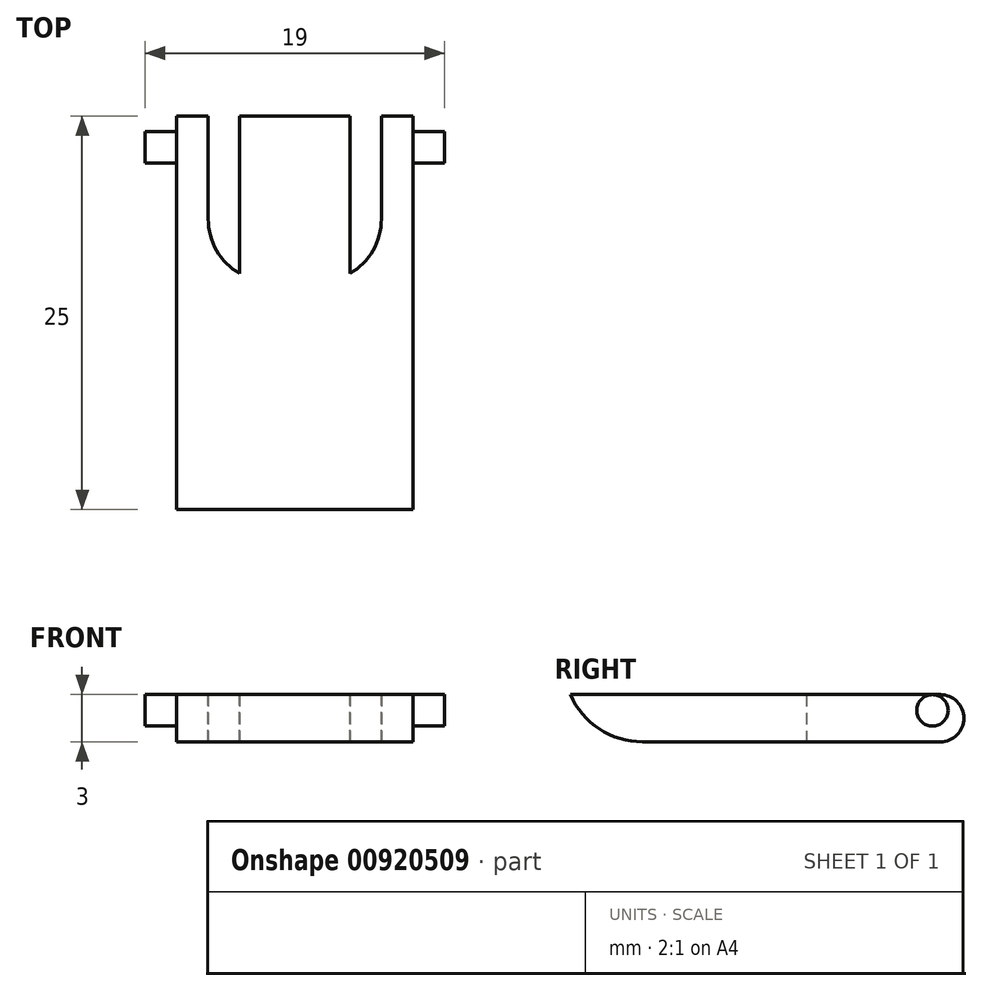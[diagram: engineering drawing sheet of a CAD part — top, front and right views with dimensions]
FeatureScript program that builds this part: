
annotation { "Feature Type Name" : "Feature", "Feature Type Description" : "" }
export const myFeature = defineFeature(function(context is Context, id is Id, definition is map)
    precondition{}
    {
        {
            var Q0;
            Q0=qCreatedBy(makeId("Top.planeOp"),FACE);
            var sketch = newSketch(context, id + "F0", { "sketchPlane" : qUnion([Q0])});
            skLineSegment(sketch, "E0", {"start": v(-7.5, -12.5) * mm, "end": v(0, -12.5) * mm});
            skLineSegment(sketch, "E1", {"start": v(0, 12.5) * mm, "end": v(-7.5, 12.5) * mm});
            skLineSegment(sketch, "E2", {"start": v(-7.5, 12.5) * mm, "end": v(-7.5, -12.5) * mm});
            skLineSegment(sketch, "E3", {"start": v(-3.5, 12.5) * mm, "end": v(-3.5, 2.5) * mm});
            skLineSegment(sketch, "E4", {"start": v(-3.5, 2.5) * mm, "end": v(-5.5, 2.5) * mm});
            skLineSegment(sketch, "E5", {"start": v(-5.5, 2.5) * mm, "end": v(-5.5, 12.5) * mm});
            skLineSegment(sketch, "E6", {"start": v(0, 12.5) * mm, "end": v(0, -12.5) * mm});
            skSolve(sketch);
        }
        {
            var Q0;
            {var subQ7=sQuery(id+"F0.wireOp",EDGE,"E0");Q0=makeQuery(id+"F0.imprint","IMPRINT",FACE,{"disambiguationData":[TD([[makeQuery(id+"F0.imprint","IMPRINT",EDGE,{"derivedFrom":subQ7}),1.0]])]});}
            var Q1;
            {var subQ0=sQuery(id+"F0.wireOp",EDGE,"XUkVxfDD-UHQ7-OXs1-Yroe-yYtnzvvzGCRX");Q1=makeQuery(id+"F0.imprint","IMPRINT",FACE,{"disambiguationData":[TD([[makeQuery(id+"F0.imprint","IMPRINT",EDGE,{"derivedFrom":subQ0}),-1.0]])]});}
            var Q2;
            Q2=sQuery(id+"F0.wireOp",EDGE,"E1");
            extrude(context, id + "F1", {"entities" : qUnion([Q0, Q1]), "surfaceEntities" : qUnion([Q2]), "depth" : 3 * mm, "offsetDistance" : 25 * mm});
        }
        {
            var Q0;
            Q0=makeQuery(id+"F1.opExtrude","SWEPT_FACE",FACE,{"disambiguationData":[OSD([sQuery(id+"F0.wireOp",EDGE,"E2")])]});
            var sketch = newSketch(context, id + "F2", { "sketchPlane" : qUnion([Q0])});
            skCircle(sketch, "E7", {"center": v(-10.5, 2) * mm, "radius": 1 * mm});
            skSolve(sketch);
        }
        {
            var Q0;
            Q0=makeQuery(id+"F2.imprint","IMPRINT",FACE,{"disambiguationData":[TD([[makeQuery(id+"F2.imprint","IMPRINT",EDGE,{"derivedFrom":sQuery(id+"F2.wireOp",EDGE,"E7")}),1.0]])]});
            extrude(context, id + "F3", {"entities" : qUnion([Q0]), "operationType" : NewBodyOperationType.ADD, "depth" : 2 * mm, "offsetDistance" : 25 * mm});
        }
        {
            var Q0;
            {var subQ0=sQuery(id+"F0.wireOp",EDGE,"E1");Q0=makeQuery(id+"F1.opExtrude","CAP_EDGE",EDGE,{"disambiguationData":[OSD([subQ0]),TDD([makeQuery(id+"F0.imprint","IMPRINT",EDGE,{"disambiguationData":[TD([[makeQuery(id+"F0.imprint","INTERSECT",VERTEX,{"derivedFrom":[subQ0,sQuery(id+"F0.wireOp",EDGE,"E2")]}),1.0]])],"derivedFrom":subQ0})])],"isStart":true});}
            var Q1;
            {var subQ0=sQuery(id+"F0.wireOp",EDGE,"E1");Q1=makeQuery(id+"F1.opExtrude","CAP_EDGE",EDGE,{"disambiguationData":[OSD([subQ0]),TDD([makeQuery(id+"F0.imprint","IMPRINT",EDGE,{"disambiguationData":[TD([[makeQuery(id+"F0.imprint","INTERSECT",VERTEX,{"derivedFrom":[subQ0,sQuery(id+"F0.wireOp",EDGE,"E2")]}),1.0]])],"derivedFrom":subQ0})])],"isStart":false});}
            var Q2;
            {var subQ0=sQuery(id+"F0.wireOp",EDGE,"E1");Q2=makeQuery(id+"F1.opExtrude","CAP_EDGE",EDGE,{"disambiguationData":[OSD([subQ0]),TDD([makeQuery(id+"F0.imprint","IMPRINT",EDGE,{"disambiguationData":[TD([[makeQuery(id+"F0.imprint","INTERSECT",VERTEX,{"derivedFrom":[subQ0,sQuery(id+"F0.wireOp",EDGE,"E6")]}),-1.0]])],"derivedFrom":subQ0})])],"isStart":true});}
            var Q3;
            {var subQ0=sQuery(id+"F0.wireOp",EDGE,"E1");Q3=makeQuery(id+"F1.opExtrude","CAP_EDGE",EDGE,{"disambiguationData":[OSD([subQ0]),TDD([makeQuery(id+"F0.imprint","IMPRINT",EDGE,{"disambiguationData":[TD([[makeQuery(id+"F0.imprint","INTERSECT",VERTEX,{"derivedFrom":[subQ0,sQuery(id+"F0.wireOp",EDGE,"E6")]}),-1.0]])],"derivedFrom":subQ0})])],"isStart":false});}
            fillet(context, id + "F4", {"entities" : qUnion([Q0, Q1, Q2, Q3]), "radius" : 1.5 * mm, "tangentPropagation" : true, "allowEdgeOverflow" : false});
        }
        {
            var Q0;
            Q0=makeQuery(id+"F1.opExtrude","SWEPT_EDGE",EDGE,{"disambiguationData":[OSD([sQuery(id+"F0.wireOp",EDGE,"E4"),sQuery(id+"F0.wireOp",EDGE,"E5")])]});
            fillet(context, id + "F5", {"entities" : qUnion([Q0]), "radius" : 4 * mm, "tangentPropagation" : true, "allowEdgeOverflow" : false});
        }
        {
            var Q0;
            Q0=makeQuery(id+"F1.opExtrude","CAP_EDGE",EDGE,{"disambiguationData":[OSD([sQuery(id+"F0.wireOp",EDGE,"E0")])],"isStart":true});
            fillet(context, id + "F6", {"entities" : qUnion([Q0]), "radius" : 5 * mm, "tangentPropagation" : true, "allowEdgeOverflow" : false});
        }
        {
            var Q0;
            Q0=makeQuery(id+"F1.opExtrude","SWEPT_BODY",BODY,{"disambiguationData":[OSD([sQuery(id+"F0.wireOp",EDGE,"E0"),sQuery(id+"F0.wireOp",EDGE,"E1"),sQuery(id+"F0.wireOp",EDGE,"E2"),sQuery(id+"F0.wireOp",EDGE,"E3"),sQuery(id+"F0.wireOp",EDGE,"E4"),sQuery(id+"F0.wireOp",EDGE,"E5"),sQuery(id+"F0.wireOp",EDGE,"E6")])]});
            var Q1;
            Q1=makeQuery(id+"F1.opExtrude","SWEPT_FACE",FACE,{"disambiguationData":[OSD([sQuery(id+"F0.wireOp",EDGE,"E6")])]});
            mirror(context, id + "F7", {"operationType" : NewBodyOperationType.ADD, "entities" : qUnion([Q0]), "mirrorPlane" : qUnion([Q1])});
        }
    });
